# Revit family: КМ Профиль_Консоль сварная KS
name_source: partatom
category: Обобщенные модели
revit_build: Autodesk Revit 2016 (Build: 20160126_1600(x64)
units: mm (PartAtom-declared; Revit-internal decimal feet)

## family parameters
Всегда вертикально = Нет
Может служить основой для арматурных стержней = Нет
На основе рабочей плоскости = Нет
Общий = Нет
При загрузке вырезать с полостями = Нет
Размер круглого соединителя = Использовать диаметр
Тип детали = Нормальный
Точка расчета площади = Нет

## types (8) — shared parameters
Мтрл.МатериалКрепленияКабельногоЛотка = <По категории>
Пр.НаименованиеКрепленияЛоткаКабельногоКанала = Консоль сварная, сталь оцинкованная по методу Сендзимира
Рзм.B = 32 мм
Рзм.B2 = 40 мм
Рзм.H1 = 32 мм
Рзм.H2 = 120 мм
Рзм.d = 8 мм
Рзм.db = 7 мм
Рзм.dl = 30 мм
Рзм.l1 = 14 мм
Рзм.s1 = 10 мм
Рзм.s2 = 50 мм
Рзм.s3 = 15 мм
Рзм.t1 = 4 мм
Спец.URLСсылкаКрепленияЛоткаКабельногоКанала = http://www.km-profil.ru
Спец.ЕдИзмКрепленияЛоткаКабельногоКанала = шт.
Спец.ИзготовительКрепленияЛоткаКабельногоКанала = КМ Профиль
Спец.НаименованиеИТенхХарКрепленияЛоткаКабельногоКанала = Консоль сварная

## per-type parameters (varying)
| type | Мсв.с | Рзм.H | Рзм.L | Рзм.t2 | Спец.КодОборудИзделияМатериалаКрепленияЛоткаКабельногоКанала | Спец.МаксимальнаяНагрузкаКрепленияЛоткаКабельногоКанала | Спец.МассаКрепленияЛоткаКабельногоКанала | Спец.МассаТекстКрепленияЛоткаКабельногоКанала |
| KS100 | 2 | 56 мм | 110 мм | 1.5 мм | KS100 | 180 | 0.30 кг | 0.30 |
| KS800 | 16 | 90 мм | 810 мм | 2 мм | KS700 | 160 | 0.72 кг | 0.72 |
| KS700 | 14 | 90 мм | 710 мм | 2 мм | KS700 | 160 | 0.72 кг | 0.72 |
| KS600 | 12 | 90 мм | 610 мм | 2 мм | KS600 | 160 | 0.72 кг | 0.72 |
| KS500 | 10 | 90 мм | 510 мм | 2 мм | KS400 | 160 | 0.72 кг | 0.72 |
| KS400 | 8 | 90 мм | 410 мм | 2 мм | KS400 | 160 | 0.72 кг | 0.72 |
| KS300 | 6 | 56 мм | 310 мм | 1.5 мм | KS300 | 140 | 0.60 кг | 0.60 |
| KS200 | 4 | 56 мм | 210 мм | 1.5 мм | KS200 | 160 | 0.39 кг | 0.39 |

## geometry (parser evidence)
native form markers: Blend x4
no freeform markers — native parametric forms only
